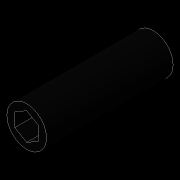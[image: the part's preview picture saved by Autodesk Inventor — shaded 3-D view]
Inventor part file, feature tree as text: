
AUTODESK INVENTOR PART (.ipt)
format: ipt  version: 2016 (Build 200138000, 138)  size: 77,824 bytes
history: native  units: in
note: dims shown in document units (in); Inventor stores cm internally (conversion verified against a paired STEP export)
features: extrude x1, sketch x1
ambient origin geometry x8: Origin, YZ Plane, XZ Plane, XY Plane, X Axis, Y Axis, Z Axis, Center Point
bodies: Solid1 (feature_tree)
feature tree (2):
  extrude  "Extrusion1"  Depth=2.0in
  sketch  "Sketch1"  dims[d0=0.375in d1=0.625in d2=2.0in d3=0.0in]
